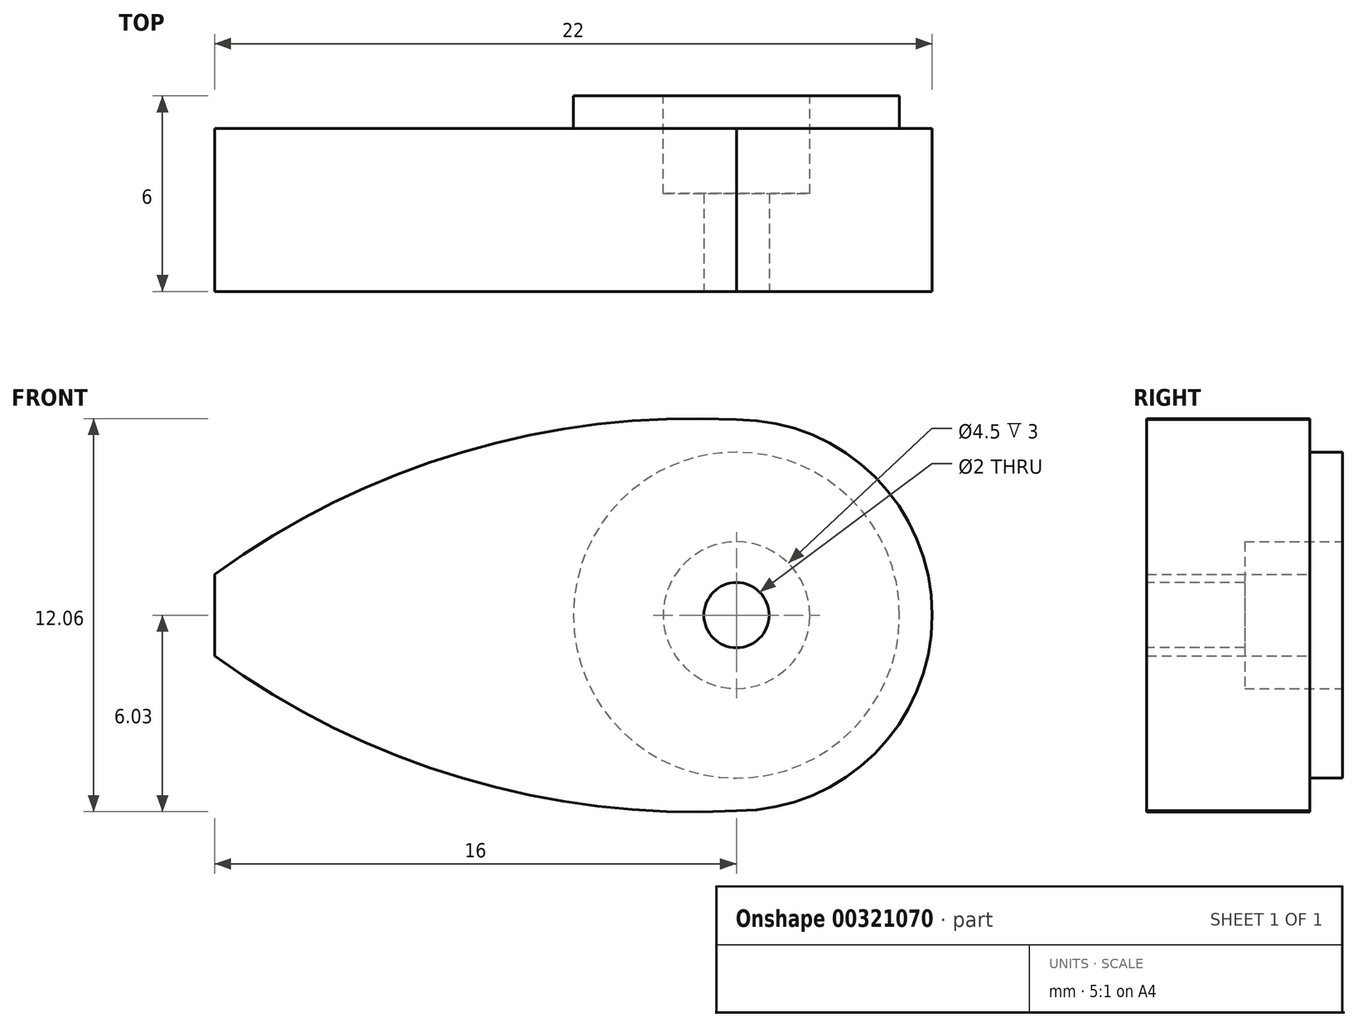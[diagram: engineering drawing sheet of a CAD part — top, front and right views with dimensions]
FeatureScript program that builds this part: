
annotation { "Feature Type Name" : "Feature", "Feature Type Description" : "" }
export const myFeature = defineFeature(function(context is Context, id is Id, definition is map)
    precondition{}
    {
        {
            var Q0;
            Q0=qCreatedBy(makeId("Front.planeOp"),FACE);
            var sketch = newSketch(context, id + "F0", { "sketchPlane" : qUnion([Q0])});
            skCircle(sketch, "E0", {"center": v(0, 0) * mm, "radius": 5 * mm});
            skSolve(sketch);
        }
        {
            var Q0;
            Q0 = qSketchRegion(id + "F0", true);
            extrude(context, id + "F1", {"entities" : qUnion([Q0]), "depth" : 1 * mm});
        }
        {
            var Q0;
            Q0=makeQuery(id+"F1.opExtrude","CAP_FACE",FACE,{"disambiguationData":[OSD([sQuery(id+"F0.wireOp",EDGE,"eqiGtoLe-QH7P-NGeF-8R8m-luKEqvCLz7Ql"),sQuery(id+"F0.wireOp",EDGE,"E0")])],"isStart":false});
            var sketch = newSketch(context, id + "F2", { "sketchPlane" : qUnion([Q0])});
            skCircle(sketch, "E1", {"center": v(0, 0) * mm, "radius": 6 * mm});
            skLineSegment(sketch, "E2", {"start": v(-6, 0) * mm, "end": v(-16, 0) * mm});
            skLineSegment(sketch, "E3.bottom", {"start": v(-16, 1.25) * mm, "end": v(4, 1.25) * mm});
            skLineSegment(sketch, "E3.top", {"start": v(-16, -1.25) * mm, "end": v(4, -1.25) * mm});
            skLineSegment(sketch, "E3.left", {"start": v(-16, 1.25) * mm, "end": v(-16, -1.25) * mm});
            skLineSegment(sketch, "E3.right", {"start": v(4, 1.25) * mm, "end": v(4, -1.25) * mm});
            skPoint(sketch, "E3.middle", {"position": v(-6, 0) * mm});
            skArc(sketch, "E4", {"start": v(0, 6) * mm, "mid": v(-8.4, 5) * mm, "end": v(-16, 1.25) * mm});
            skArc(sketch, "E5", {"start": v(-16, -1.25) * mm, "mid": v(-8.4, -5) * mm, "end": v(0, -6) * mm});
            skSolve(sketch);
        }
        {
            var Q0;
            Q0 = qSketchRegion(id + "F2", true);
            extrude(context, id + "F3", {"entities" : qUnion([Q0]), "operationType" : NewBodyOperationType.ADD, "depth" : 5 * mm});
        }
        {
            var Q0;
            Q0=makeQuery(id+"F3.opExtrude","CAP_FACE",FACE,{"disambiguationData":[OSD([sQuery(id+"F2.wireOp",EDGE,"E1"),sQuery(id+"F2.wireOp",EDGE,"E3.bottom"),sQuery(id+"F2.wireOp",EDGE,"E3.top"),sQuery(id+"F2.wireOp",EDGE,"E3.left"),sQuery(id+"F2.wireOp",EDGE,"E3.right"),sQuery(id+"F2.wireOp",EDGE,"E4"),sQuery(id+"F2.wireOp",EDGE,"E5")])],"isStart":false});
            var sketch = newSketch(context, id + "F4", { "sketchPlane" : qUnion([Q0])});
            skLineSegment(sketch, "E6.bottom", {"start": v(-6.69, 1.86) * mm, "end": v(4.64, 1.86) * mm});
            skLineSegment(sketch, "E6.top", {"start": v(-6.69, -1.88) * mm, "end": v(4.64, -1.88) * mm});
            skLineSegment(sketch, "E6.left", {"start": v(-6.69, 1.86) * mm, "end": v(-6.69, -1.88) * mm});
            skLineSegment(sketch, "E6.right", {"start": v(4.64, 1.86) * mm, "end": v(4.64, -1.88) * mm});
            skSolve(sketch);
        }
        {
            var Q0;
            Q0 = qSketchRegion(id + "F4", true);
            extrude(context, id + "F5", {"entities" : qUnion([Q0]), "operationType" : NewBodyOperationType.ADD, "oppositeDirection" : true, "depth" : 5 * mm});
        }
        {
            var Q0;
            Q0=makeQuery(id+"F1.opExtrude","CAP_FACE",FACE,{"disambiguationData":[OSD([sQuery(id+"F0.wireOp",EDGE,"E0")])],"isStart":true});
            var sketch = newSketch(context, id + "F6", { "sketchPlane" : qUnion([Q0])});
            skCircle(sketch, "E7", {"center": v(0, 0) * mm, "radius": 2.25 * mm});
            skSolve(sketch);
        }
        {
            var Q0;
            Q0 = qSketchRegion(id + "F6", true);
            extrude(context, id + "F7", {"entities" : qUnion([Q0]), "operationType" : NewBodyOperationType.REMOVE, "oppositeDirection" : true, "depth" : 3 * mm});
        }
        {
            var Q0;
            Q0=makeQuery(id+"F5.boolean.opBoolean","MERGE",FACE,{"derivedFrom":[makeQuery(id+"F3.opExtrude","CAP_FACE",FACE,{"disambiguationData":[OSD([sQuery(id+"F2.wireOp",EDGE,"E1"),sQuery(id+"F2.wireOp",EDGE,"E3.bottom"),sQuery(id+"F2.wireOp",EDGE,"E3.top"),sQuery(id+"F2.wireOp",EDGE,"E3.left"),sQuery(id+"F2.wireOp",EDGE,"E3.right"),sQuery(id+"F2.wireOp",EDGE,"E4"),sQuery(id+"F2.wireOp",EDGE,"E5")])],"isStart":false}),makeQuery(id+"F5.opExtrude","CAP_FACE",FACE,{"disambiguationData":[OSD([sQuery(id+"F4.wireOp",EDGE,"E6.bottom"),sQuery(id+"F4.wireOp",EDGE,"E6.top"),sQuery(id+"F4.wireOp",EDGE,"E6.left"),sQuery(id+"F4.wireOp",EDGE,"E6.right")])],"isStart":true})]});
            var sketch = newSketch(context, id + "F8", { "sketchPlane" : qUnion([Q0])});
            skCircle(sketch, "E8", {"center": v(0, 0) * mm, "radius": 1 * mm});
            skSolve(sketch);
        }
        {
            var Q0;
            Q0 = qSketchRegion(id + "F8", true);
            extrude(context, id + "F9", {"entities" : qUnion([Q0]), "operationType" : NewBodyOperationType.REMOVE, "oppositeDirection" : true, "depth" : 25 * mm});
        }
    });
